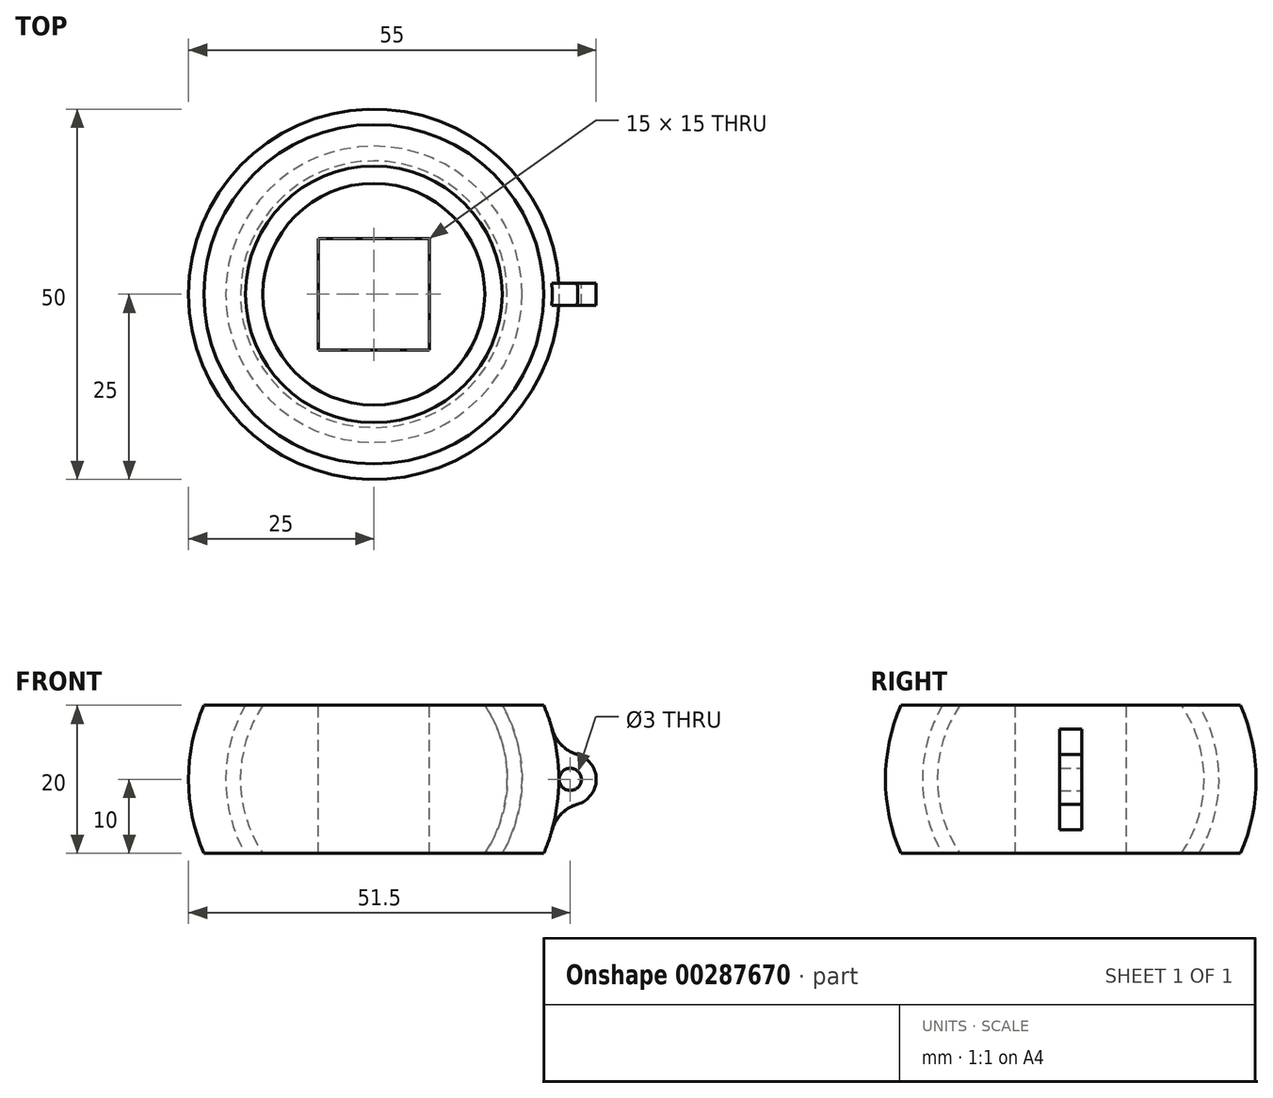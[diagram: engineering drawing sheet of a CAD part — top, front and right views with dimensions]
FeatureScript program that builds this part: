
annotation { "Feature Type Name" : "Feature", "Feature Type Description" : "" }
export const myFeature = defineFeature(function(context is Context, id is Id, definition is map)
    precondition{}
    {
        {
            var Q0;
            Q0=qCreatedBy(makeId("Top.planeOp"),FACE);
            var sketch = newSketch(context, id + "F0", { "sketchPlane" : qUnion([Q0])});
            skCircle(sketch, "E0", {"center": v(0, 0) * mm, "radius": 25 * mm});
            skSolve(sketch);
        }
        {
            var Q0;
            Q0=makeQuery(id+"F0.imprint","IMPRINT",FACE,{"disambiguationData":[TD([[makeQuery(id+"F0.imprint","IMPRINT",EDGE,{"derivedFrom":sQuery(id+"F0.wireOp",EDGE,"E0")}),1.0]])]});
            extrude(context, id + "F1", {"entities" : qUnion([Q0]), "endBound" : BoundingType.SYMMETRIC, "depth" : 20 * mm});
        }
        {
            var Q0;
            Q0=makeQuery(id+"F1.opExtrude","CAP_FACE",FACE,{"disambiguationData":[OSD([sQuery(id+"F0.wireOp",EDGE,"E0")])],"isStart":false});
            var sketch = newSketch(context, id + "F2", { "sketchPlane" : qUnion([Q0])});
            skLineSegment(sketch, "E1.bottom", {"start": v(-7.5, 7.5) * mm, "end": v(7.5, 7.5) * mm});
            skLineSegment(sketch, "E1.top", {"start": v(-7.5, -7.5) * mm, "end": v(7.5, -7.5) * mm});
            skLineSegment(sketch, "E1.left", {"start": v(-7.5, 7.5) * mm, "end": v(-7.5, -7.5) * mm});
            skLineSegment(sketch, "E1.right", {"start": v(7.5, 7.5) * mm, "end": v(7.5, -7.5) * mm});
            skPoint(sketch, "E1.middle", {"position": v(0, 0) * mm});
            skSolve(sketch);
        }
        {
            var Q0;
            Q0=makeQuery(id+"F2.imprint","IMPRINT",FACE,{"disambiguationData":[TD([[makeQuery(id+"F2.imprint","IMPRINT",EDGE,{"derivedFrom":sQuery(id+"F2.wireOp",EDGE,"E1.bottom")}),-1.0]])]});
            extrude(context, id + "F3", {"entities" : qUnion([Q0]), "operationType" : NewBodyOperationType.REMOVE, "endBound" : BoundingType.THROUGH_ALL, "oppositeDirection" : true, "depth" : 20 * mm});
        }
        {
            var Q0;
            Q0=qCreatedBy(makeId("Front.planeOp"),FACE);
            var sketch = newSketch(context, id + "F4", { "sketchPlane" : qUnion([Q0])});
            skLineSegment(sketch, "E2.0.0", {"start": v(-25, 10) * mm, "end": v(-22.91, 10) * mm, "construction": true});
            skLineSegment(sketch, "E3.0", {"start": v(-25, -10) * mm, "end": v(-22.91, -10) * mm, "construction": true});
            skLineSegment(sketch, "E4.trimOffspring", {"start": v(22.91, 10) * mm, "end": v(25, 10) * mm, "construction": true});
            skLineSegment(sketch, "E5.trimOffspring", {"start": v(22.91, -10) * mm, "end": v(25, -10) * mm, "construction": true});
            skLineSegment(sketch, "E6", {"start": v(-22.91, 10) * mm, "end": v(-65, 10) * mm});
            skLineSegment(sketch, "E7", {"start": v(-22.91, -10) * mm, "end": v(-65, -10) * mm});
            skLineSegment(sketch, "E8", {"start": v(-65, -10) * mm, "end": v(-65, 10) * mm});
            skLineSegment(sketch, "E9", {"start": v(0, 0) * mm, "end": v(0, 65.14) * mm, "construction": true});
            skArc(sketch, "E10", {"start": v(-22.91, 10) * mm, "mid": v(-25, 0) * mm, "end": v(-22.91, -10) * mm});
            skSolve(sketch);
        }
        {
            var Q0;
            Q0=makeQuery(id+"F4.imprint","IMPRINT",FACE,{"disambiguationData":[TD([[makeQuery(id+"F4.imprint","IMPRINT",EDGE,{"derivedFrom":sQuery(id+"F4.wireOp",EDGE,"E6")}),1.0]])]});
            var Q1;
            Q1=sQuery(id+"F4.wireOp",EDGE,"E9");
            revolve(context, id + "F5", {"operationType" : NewBodyOperationType.REMOVE, "entities" : qUnion([Q0]), "axis" : qUnion([Q1]), "revolveType" : RevolveType.FULL, "oppositeDirection" : true});
        }
        {
            var Q0;
            Q0=qCreatedBy(makeId("Front.planeOp"),FACE);
            var sketch = newSketch(context, id + "F6", { "sketchPlane" : qUnion([Q0])});
            skArc(sketch, "E11", {"start": v(0, 20) * mm, "mid": v(-20, 0) * mm, "end": v(0, -20) * mm});
            skArc(sketch, "E12.0", {"start": v(0, 18) * mm, "mid": v(-18, 0) * mm, "end": v(0, -18) * mm});
            skLineSegment(sketch, "E13", {"start": v(0, 35.29) * mm, "end": v(0, -40.35) * mm, "construction": true});
            skLineSegment(sketch, "E14", {"start": v(0, 20) * mm, "end": v(0, 18) * mm});
            skLineSegment(sketch, "E15", {"start": v(0, -18) * mm, "end": v(0, -20) * mm});
            skSolve(sketch);
        }
        {
            var Q0;
            Q0=makeQuery(id+"F6.imprint","IMPRINT",FACE,{"disambiguationData":[TD([[makeQuery(id+"F6.imprint","IMPRINT",EDGE,{"derivedFrom":sQuery(id+"F6.wireOp",EDGE,"E11")}),1.0]])]});
            var Q1;
            Q1=sQuery(id+"F6.wireOp",EDGE,"E13");
            revolve(context, id + "F7", {"operationType" : NewBodyOperationType.REMOVE, "entities" : qUnion([Q0]), "axis" : qUnion([Q1]), "revolveType" : RevolveType.FULL, "oppositeDirection" : true});
        }
        {
            var Q0;
            Q0=qCreatedBy(makeId("Front.planeOp"),FACE);
            var sketch = newSketch(context, id + "F8", { "sketchPlane" : qUnion([Q0])});
            skCircle(sketch, "E16", {"center": v(26.5, 0) * mm, "radius": 1.5 * mm});
            skCircle(sketch, "E17.0", {"center": v(26.5, 0) * mm, "radius": 3.5 * mm});
            skArc(sketch, "E18", {"start": v(-22.91, 10) * mm, "mid": v(0, -25) * mm, "end": v(22.91, 10) * mm, "construction": true});
            skSolve(sketch);
        }
        {
            var Q0;
            Q0=makeQuery(id+"F8.imprint","IMPRINT",FACE,{"disambiguationData":[TD([[makeQuery(id+"F8.imprint","IMPRINT",EDGE,{"derivedFrom":sQuery(id+"F8.wireOp",EDGE,"E16")}),-1.0]])]});
            extrude(context, id + "F9", {"entities" : qUnion([Q0]), "operationType" : NewBodyOperationType.ADD, "endBound" : BoundingType.SYMMETRIC, "depth" : 3 * mm});
        }
        {
            var Q0;
            Q0=makeQuery(id+"F9.boolean.opBoolean","INTERSECT",EDGE,{"disambiguationData":[OD(1.0)],"derivedFrom":[makeQuery(id+"F5.boolean.opBoolean","COPY",FACE,{"derivedFrom":makeQuery(id+"F5.opRevolve","SWEPT_FACE",FACE,{"disambiguationData":[OSD([sQuery(id+"F4.wireOp",EDGE,"E10")])]})}),makeQuery(id+"F9.opExtrude","SWEPT_FACE",FACE,{"disambiguationData":[OSD([sQuery(id+"F8.wireOp",EDGE,"E17.0")])]})]});
            var Q1;
            Q1=makeQuery(id+"F9.boolean.opBoolean","INTERSECT",EDGE,{"disambiguationData":[OD(0.0)],"derivedFrom":[makeQuery(id+"F5.boolean.opBoolean","COPY",FACE,{"derivedFrom":makeQuery(id+"F5.opRevolve","SWEPT_FACE",FACE,{"disambiguationData":[OSD([sQuery(id+"F4.wireOp",EDGE,"E10")])]})}),makeQuery(id+"F9.opExtrude","SWEPT_FACE",FACE,{"disambiguationData":[OSD([sQuery(id+"F8.wireOp",EDGE,"E17.0")])]})]});
            fillet(context, id + "F10", {"entities" : qUnion([Q0, Q1]), "radius" : 5 * mm, "tangentPropagation" : true, "allowEdgeOverflow" : false});
        }
    });
